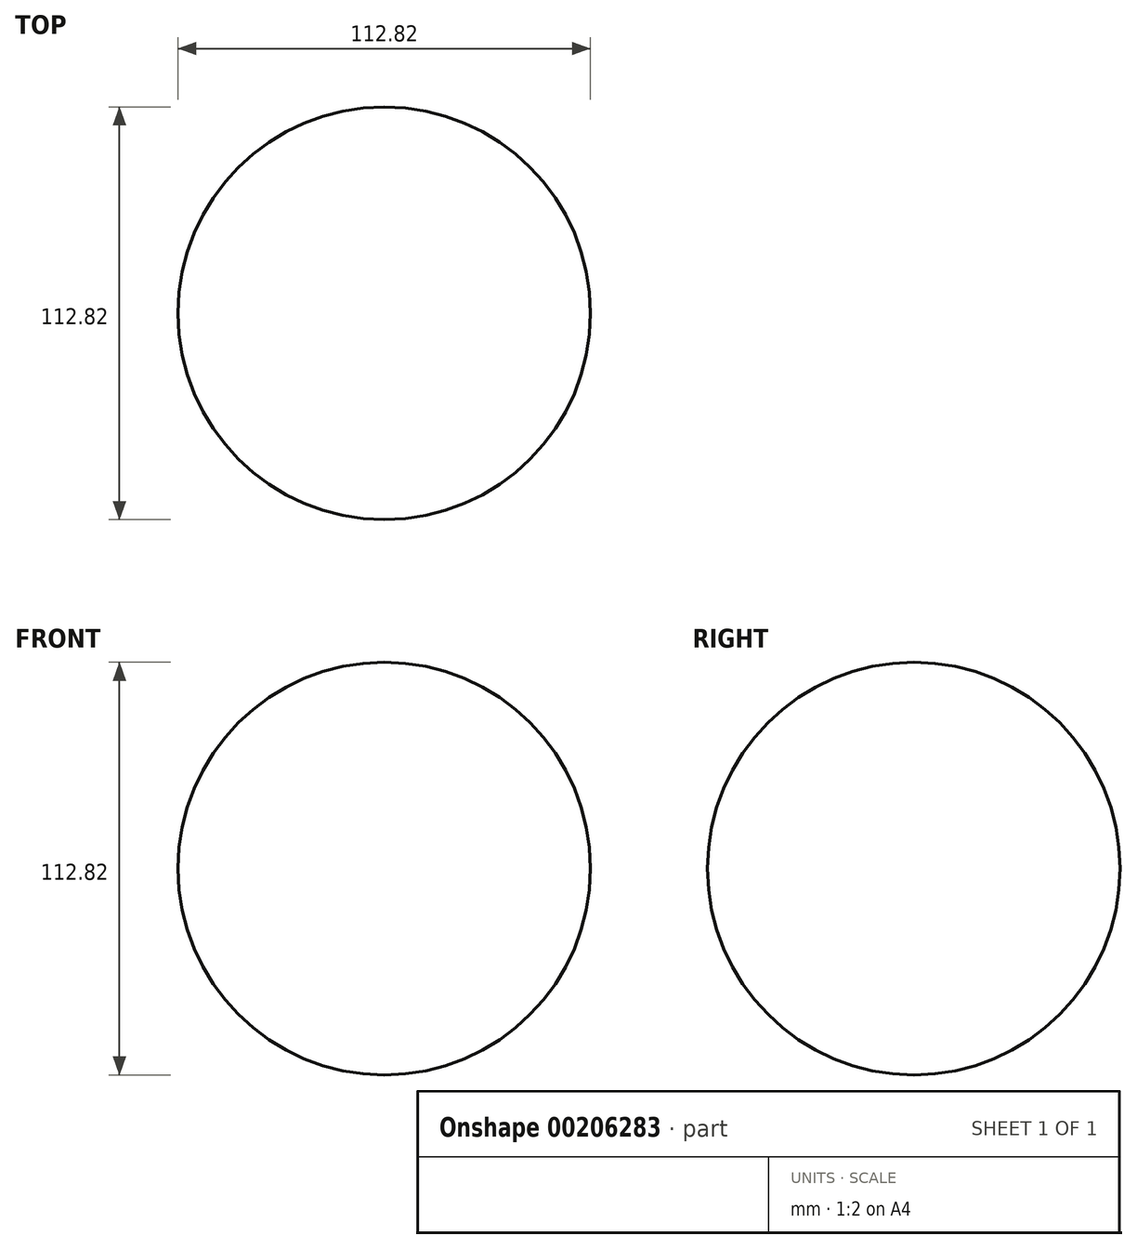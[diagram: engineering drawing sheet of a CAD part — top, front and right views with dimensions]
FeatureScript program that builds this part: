
annotation { "Feature Type Name" : "Feature", "Feature Type Description" : "" }
export const myFeature = defineFeature(function(context is Context, id is Id, definition is map)
    precondition{}
    {
        {
            var Q0;
            Q0=qCreatedBy(makeId("Front.planeOp"),FACE);
            var sketch = newSketch(context, id + "F0", { "sketchPlane" : qUnion([Q0])});
            skLineSegment(sketch, "E0", {"start": v(-121, 0) * mm, "end": v(100.6, 0) * mm});
            skCircle(sketch, "E1", {"center": v(0, 0) * mm, "radius": 56.4 * mm});
            skSolve(sketch);
        }
        {
            var Q0;
            {var subQ0=sQuery(id+"F0.wireOp",EDGE,"E1");var subQ1=sQuery(id+"F0.wireOp",EDGE,"E0");var subQ2=makeQuery(id+"F0.imprint","INTERSECT",VERTEX,{"disambiguationData":[OD(0.0)],"derivedFrom":[subQ1,subQ0]});Q0=makeQuery(id+"F0.imprint","IMPRINT",FACE,{"disambiguationData":[TD([[makeQuery(id+"F0.imprint","IMPRINT",EDGE,{"disambiguationData":[TD([[subQ2,-1.0]])],"derivedFrom":subQ1}),1.0]])]});}
            var Q1;
            Q1=sQuery(id+"F0.wireOp",EDGE,"E0");
            revolve(context, id + "F1", {"entities" : qUnion([Q0]), "axis" : qUnion([Q1]), "revolveType" : RevolveType.FULL});
        }
    });
